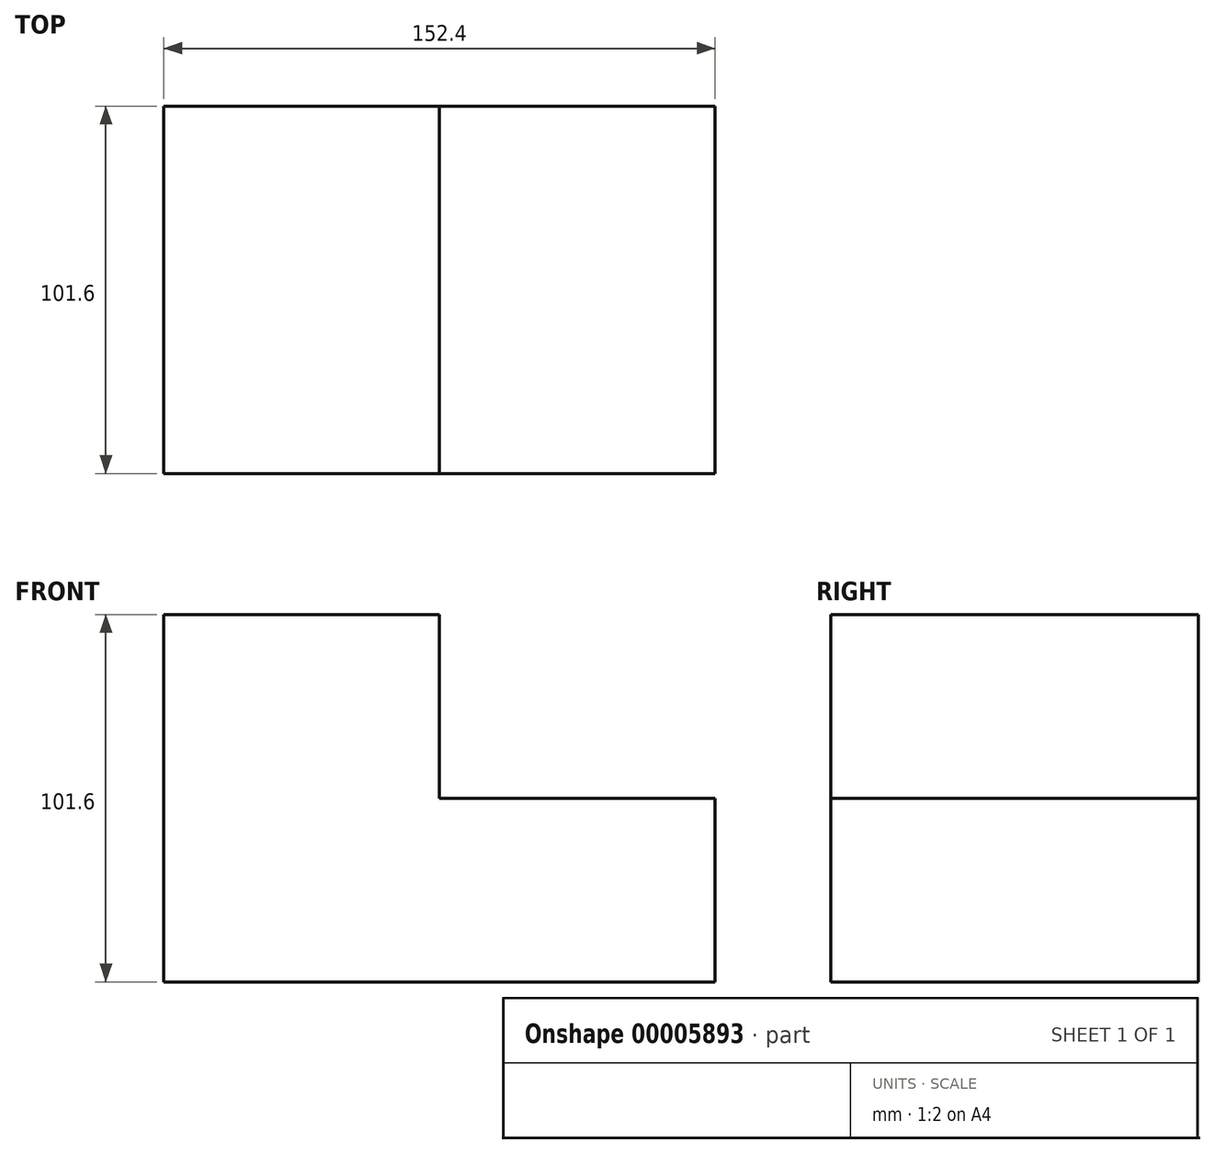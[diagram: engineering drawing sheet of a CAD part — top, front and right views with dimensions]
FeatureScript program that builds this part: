
annotation { "Feature Type Name" : "Feature", "Feature Type Description" : "" }
export const myFeature = defineFeature(function(context is Context, id is Id, definition is map)
    precondition{}
    {
        {
            var Q0;
            Q0=qCreatedBy(makeId("Front.planeOp"),FACE);
            var sketch = newSketch(context, id + "F0", { "sketchPlane" : qUnion([Q0])});
            skLineSegment(sketch, "E0", {"start": v(0, 0) * mm, "end": v(152.4, 0) * mm});
            skLineSegment(sketch, "E1", {"start": v(152.4, 0) * mm, "end": v(152.4, 50.8) * mm});
            skLineSegment(sketch, "E2", {"start": v(152.4, 50.8) * mm, "end": v(76.2, 50.8) * mm});
            skLineSegment(sketch, "E3", {"start": v(76.2, 50.8) * mm, "end": v(76.2, 101.6) * mm});
            skLineSegment(sketch, "E4", {"start": v(76.2, 101.6) * mm, "end": v(0, 101.6) * mm});
            skLineSegment(sketch, "E5", {"start": v(0, 101.6) * mm, "end": v(0, 0) * mm});
            skSolve(sketch);
        }
        {
            var Q0;
            Q0=makeQuery(id+"F0.imprint","IMPRINT",FACE,{"disambiguationData":[TD([[makeQuery(id+"F0.imprint","IMPRINT",EDGE,{"derivedFrom":sQuery(id+"F0.wireOp",EDGE,"E0")}),1.0]])]});
            extrude(context, id + "F1", {"entities" : qUnion([Q0]), "depth" : 101.6 * mm});
        }
    });
